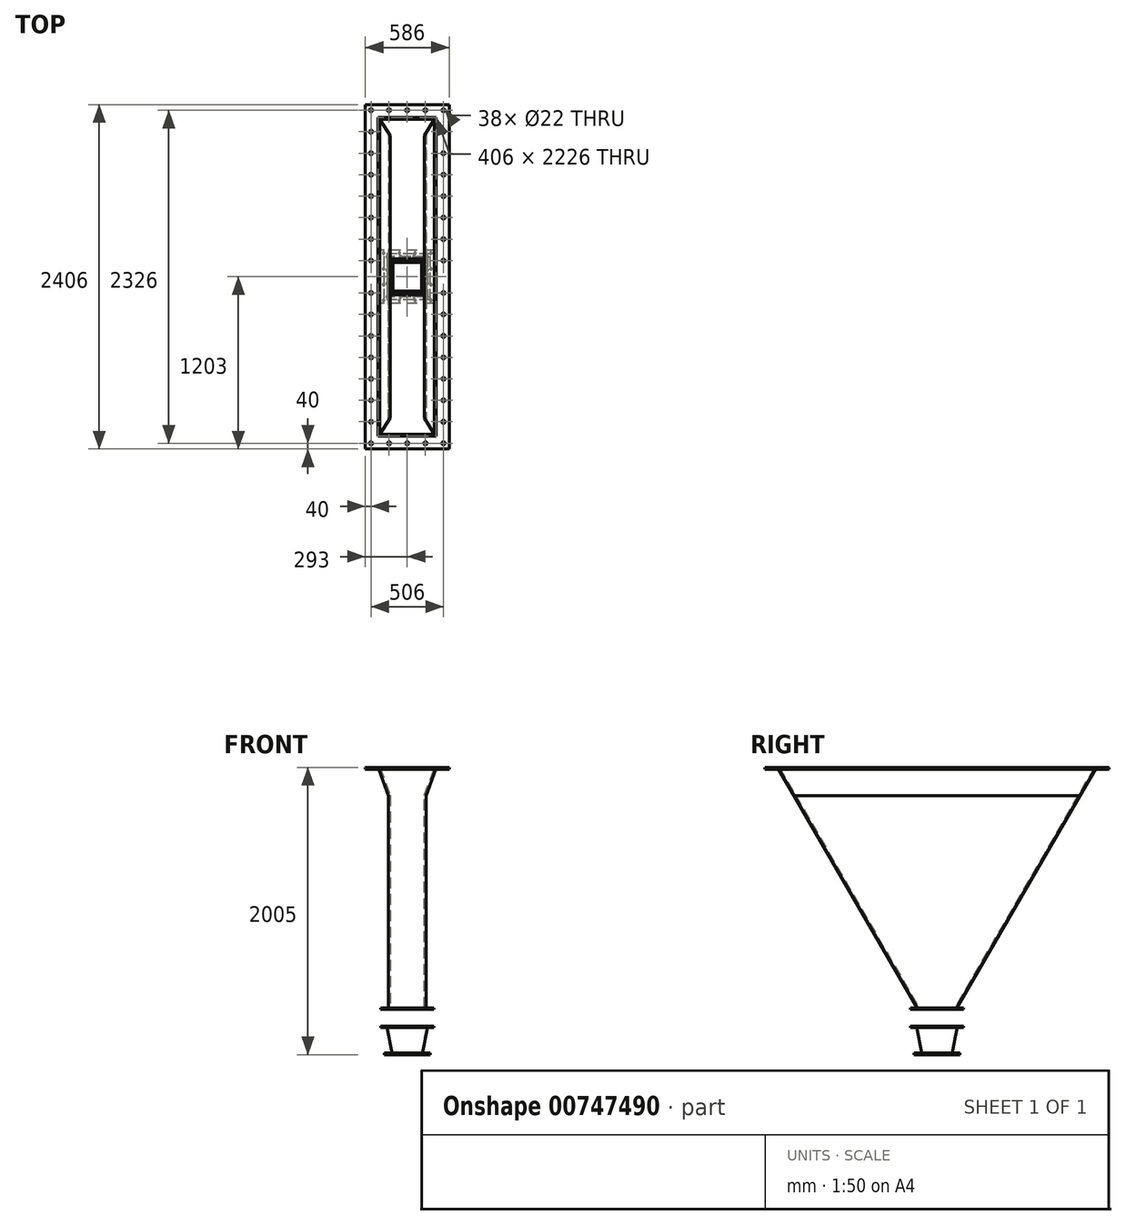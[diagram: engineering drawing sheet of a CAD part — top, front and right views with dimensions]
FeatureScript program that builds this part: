
annotation { "Feature Type Name" : "Feature", "Feature Type Description" : "" }
export const myFeature = defineFeature(function(context is Context, id is Id, definition is map)
    precondition{}
    {
        {
            var Q0;
            Q0=qCreatedBy(makeId("Front.planeOp"),FACE);
            var sketch = newSketch(context, id + "F0", { "sketchPlane" : qUnion([Q0])});
            skLineSegment(sketch, "E0", {"start": v(-203, 0) * mm, "end": v(203, 0) * mm});
            skLineSegment(sketch, "E1", {"start": v(0, 0) * mm, "end": v(0, -195.07) * mm, "construction": true});
            skLineSegment(sketch, "E2", {"start": v(-132, -195.07) * mm, "end": v(132, -195.07) * mm});
            skLineSegment(sketch, "E3", {"start": v(-203, 0) * mm, "end": v(-132, -195.07) * mm});
            skLineSegment(sketch, "E4", {"start": v(132, -195.07) * mm, "end": v(203, 0) * mm});
            skLineSegment(sketch, "E5", {"start": v(-132, -195.07) * mm, "end": v(-132, -1690) * mm});
            skLineSegment(sketch, "E6", {"start": v(-132, -1690) * mm, "end": v(132, -1690) * mm});
            skLineSegment(sketch, "E7", {"start": v(132, -1690) * mm, "end": v(132, -195.07) * mm});
            skLineSegment(sketch, "E8", {"start": v(-132, -195.07) * mm, "end": v(-132, 0) * mm, "construction": true});
            skLineSegment(sketch, "E9", {"start": v(132, -195.07) * mm, "end": v(132, 0) * mm, "construction": true});
            skSolve(sketch);
        }
        {
            var Q0;
            Q0=makeQuery(id+"F0.imprint","IMPRINT",FACE,{"disambiguationData":[TD([[makeQuery(id+"F0.imprint","IMPRINT",EDGE,{"derivedFrom":sQuery(id+"F0.wireOp",EDGE,"E0")}),-1.0]])]});
            var Q1;
            Q1=makeQuery(id+"F0.imprint","IMPRINT",FACE,{"disambiguationData":[TD([[makeQuery(id+"F0.imprint","IMPRINT",EDGE,{"derivedFrom":sQuery(id+"F0.wireOp",EDGE,"E2")}),-1.0]])]});
            extrude(context, id + "F1", {"entities" : qUnion([Q0, Q1]), "endBound" : BoundingType.SYMMETRIC, "oppositeDirection" : true, "depth" : 2226 * mm, "offsetDistance" : 25 * mm});
        }
        {
            var Q0;
            Q0=makeQuery(id+"F1.opExtrude","SWEPT_FACE",FACE,{"disambiguationData":[OSD([sQuery(id+"F0.wireOp",EDGE,"E7")])]});
            var sketch = newSketch(context, id + "F2", { "sketchPlane" : qUnion([Q0])});
            skLineSegment(sketch, "E10", {"start": v(0, -1690) * mm, "end": v(0, -1167.4) * mm, "construction": true});
            skLineSegment(sketch, "E11", {"start": v(0, -1690) * mm, "end": v(132, -1690) * mm});
            skLineSegment(sketch, "E12", {"start": v(132, -1690) * mm, "end": v(1113, 0) * mm});
            skLineSegment(sketch, "E13", {"start": v(1113, 0) * mm, "end": v(1113, -1690) * mm});
            skLineSegment(sketch, "E14", {"start": v(1113, -1690) * mm, "end": v(132, -1690) * mm});
            skLineSegment(sketch, "E15.MirrorCS", {"start": v(-132, -1690) * mm, "end": v(-1113, 0) * mm});
            skLineSegment(sketch, "E16.MirrorCS", {"start": v(-1113, -1690) * mm, "end": v(-132, -1690) * mm});
            skLineSegment(sketch, "E17.MirrorCS", {"start": v(-1113, 0) * mm, "end": v(-1113, -1690) * mm});
            skSolve(sketch);
        }
        {
            var Q0;
            Q0=qSketchRegion(id+"F2",true);
            extrude(context, id + "F3", {"entities" : qUnion([Q0]), "operationType" : NewBodyOperationType.REMOVE, "oppositeDirection" : true, "depth" : 400 * mm, "offsetDistance" : 25 * mm, "hasSecondDirection" : true, "secondDirectionOppositeDirection" : false, "secondDirectionDepth" : 400 * mm});
        }
        {
            var Q0;
            Q0=makeQuery(id+"F1.opExtrude","SWEPT_FACE",FACE,{"disambiguationData":[OSD([sQuery(id+"F0.wireOp",EDGE,"E0")])]});
            shell(context, id + "F4", {"entities" : qUnion([Q0]), "thickness" : 12 * mm});
        }
        {
            var Q0;
            Q0=makeQuery(id+"F1.opExtrude","SWEPT_FACE",FACE,{"disambiguationData":[OSD([sQuery(id+"F0.wireOp",EDGE,"E6")])]});
            var sketch = newSketch(context, id + "F5", { "sketchPlane" : qUnion([Q0])});
            skLineSegment(sketch, "E18.bottom", {"start": v(-120, 120) * mm, "end": v(120, 120) * mm});
            skLineSegment(sketch, "E18.top", {"start": v(-120, -120) * mm, "end": v(120, -120) * mm});
            skLineSegment(sketch, "E18.left", {"start": v(-120, 120) * mm, "end": v(-120, -120) * mm});
            skLineSegment(sketch, "E18.right", {"start": v(120, 120) * mm, "end": v(120, -120) * mm});
            skPoint(sketch, "E18.middle", {"position": v(0, 0) * mm});
            skPoint(sketch, "E18.middle.positionSnap0", {"position": v(132, 0) * mm});
            skPoint(sketch, "E18.middle.positionSnap1", {"position": v(0, -132) * mm});
            skPoint(sketch, "E18.centerSnap0", {"position": v(132, 0) * mm});
            skPoint(sketch, "E18.centerSnap1", {"position": v(0, -132) * mm});
            skSolve(sketch);
        }
        {
            var Q0;
            Q0=qSketchRegion(id+"F5",true);
            extrude(context, id + "F6", {"entities" : qUnion([Q0]), "operationType" : NewBodyOperationType.REMOVE, "endBound" : BoundingType.THROUGH_ALL, "oppositeDirection" : true, "depth" : 25 * mm, "offsetDistance" : 25 * mm});
        }
        {
            var Q0;
            Q0=makeQuery(id+"F1.opExtrude","SWEPT_FACE",FACE,{"disambiguationData":[OSD([sQuery(id+"F0.wireOp",EDGE,"E0")])]});
            var sketch = newSketch(context, id + "F7", { "sketchPlane" : qUnion([Q0])});
            skLineSegment(sketch, "E19.bottom", {"start": v(-203, -1113) * mm, "end": v(203, -1113) * mm});
            skLineSegment(sketch, "E19.top", {"start": v(-203, 1113) * mm, "end": v(203, 1113) * mm});
            skLineSegment(sketch, "E19.left", {"start": v(-203, -1113) * mm, "end": v(-203, 1113) * mm});
            skLineSegment(sketch, "E19.right", {"start": v(203, -1113) * mm, "end": v(203, 1113) * mm});
            skLineSegment(sketch, "E20.bottom", {"start": v(-293, 1203) * mm, "end": v(293, 1203) * mm});
            skLineSegment(sketch, "E20.top", {"start": v(-293, -1203) * mm, "end": v(293, -1203) * mm});
            skLineSegment(sketch, "E20.left", {"start": v(-293, 1203) * mm, "end": v(-293, -1203) * mm});
            skLineSegment(sketch, "E20.right", {"start": v(293, 1203) * mm, "end": v(293, -1203) * mm});
            skPoint(sketch, "E20.middle", {"position": v(0, 0) * mm});
            skPoint(sketch, "E20.middle.positionSnap0", {"position": v(-203, 0) * mm});
            skPoint(sketch, "E20.middle.positionSnap1", {"position": v(0, -1099.12) * mm});
            skPoint(sketch, "E20.centerSnap0", {"position": v(-203, 0) * mm});
            skPoint(sketch, "E20.centerSnap1", {"position": v(0, -1099.12) * mm});
            skCircle(sketch, "E21", {"center": v(0, -1163) * mm, "radius": 11 * mm});
            skCircle(sketch, "E22", {"center": v(127, -1163) * mm, "radius": 11 * mm});
            skCircle(sketch, "E23", {"center": v(253, -1163) * mm, "radius": 11 * mm});
            skCircle(sketch, "E24", {"center": v(253, -1013) * mm, "radius": 11 * mm});
            skCircle(sketch, "E25", {"center": v(253, -113) * mm, "radius": 11 * mm});
            skCircle(sketch, "E26", {"center": v(253, -263) * mm, "radius": 11 * mm});
            skCircle(sketch, "E27", {"center": v(253, -413) * mm, "radius": 11 * mm});
            skCircle(sketch, "E28", {"center": v(253, -563) * mm, "radius": 11 * mm});
            skCircle(sketch, "E29", {"center": v(253, -713) * mm, "radius": 11 * mm});
            skCircle(sketch, "E30", {"center": v(253, -863) * mm, "radius": 11 * mm});
            skLineSegment(sketch, "E31", {"start": v(0, 0) * mm, "end": v(-353.58, 0) * mm, "construction": true});
            skCircle(sketch, "E32.MirrorC", {"center": v(253, 113) * mm, "radius": 11 * mm});
            skCircle(sketch, "E33.MirrorC", {"center": v(253, 263) * mm, "radius": 11 * mm});
            skCircle(sketch, "E34.MirrorC", {"center": v(253, 413) * mm, "radius": 11 * mm});
            skCircle(sketch, "E35.MirrorC", {"center": v(253, 563) * mm, "radius": 11 * mm});
            skCircle(sketch, "E36.MirrorC", {"center": v(253, 713) * mm, "radius": 11 * mm});
            skCircle(sketch, "E37.MirrorC", {"center": v(253, 863) * mm, "radius": 11 * mm});
            skCircle(sketch, "E38.MirrorC", {"center": v(253, 1013) * mm, "radius": 11 * mm});
            skCircle(sketch, "E39.MirrorC", {"center": v(253, 1163) * mm, "radius": 11 * mm});
            skCircle(sketch, "E40.MirrorC", {"center": v(127, 1163) * mm, "radius": 11 * mm});
            skCircle(sketch, "E41.MirrorC", {"center": v(0, 1163) * mm, "radius": 11 * mm});
            skLineSegment(sketch, "E42", {"start": v(0, 1028.55) * mm, "end": v(0, 1182.62) * mm, "construction": true});
            skCircle(sketch, "E43.MirrorC", {"center": v(-127, 1163) * mm, "radius": 11 * mm});
            skCircle(sketch, "E44.MirrorC", {"center": v(-253, 1163) * mm, "radius": 11 * mm});
            skCircle(sketch, "E45.MirrorC", {"center": v(-253, 1013) * mm, "radius": 11 * mm});
            skCircle(sketch, "E46.MirrorC", {"center": v(-253, 863) * mm, "radius": 11 * mm});
            skCircle(sketch, "E47.MirrorC", {"center": v(-253, 713) * mm, "radius": 11 * mm});
            skCircle(sketch, "E48.MirrorC", {"center": v(-253, 563) * mm, "radius": 11 * mm});
            skCircle(sketch, "E49.MirrorC", {"center": v(-253, 413) * mm, "radius": 11 * mm});
            skCircle(sketch, "E50.MirrorC", {"center": v(-253, 263) * mm, "radius": 11 * mm});
            skCircle(sketch, "E51.MirrorC", {"center": v(-253, 113) * mm, "radius": 11 * mm});
            skCircle(sketch, "E52.MirrorC", {"center": v(-253, -113) * mm, "radius": 11 * mm});
            skCircle(sketch, "E53.MirrorC", {"center": v(-253, -263) * mm, "radius": 11 * mm});
            skCircle(sketch, "E54.MirrorC", {"center": v(-253, -413) * mm, "radius": 11 * mm});
            skCircle(sketch, "E55.MirrorC", {"center": v(-253, -563) * mm, "radius": 11 * mm});
            skCircle(sketch, "E56.MirrorC", {"center": v(-253, -713) * mm, "radius": 11 * mm});
            skCircle(sketch, "E57.MirrorC", {"center": v(-253, -863) * mm, "radius": 11 * mm});
            skCircle(sketch, "E58.MirrorC", {"center": v(-253, -1013) * mm, "radius": 11 * mm});
            skCircle(sketch, "E59.MirrorC", {"center": v(-253, -1163) * mm, "radius": 11 * mm});
            skCircle(sketch, "E60.MirrorC", {"center": v(-127, -1163) * mm, "radius": 11 * mm});
            skSolve(sketch);
        }
        {
            var Q0;
            Q0=qSketchRegion(id+"F7",true);
            extrude(context, id + "F8", {"entities" : qUnion([Q0]), "operationType" : NewBodyOperationType.ADD, "oppositeDirection" : true, "depth" : 12 * mm, "offsetDistance" : 25 * mm});
        }
        {
            var Q0;
            Q0=makeQuery(id+"F1.opExtrude","SWEPT_FACE",FACE,{"disambiguationData":[OSD([sQuery(id+"F0.wireOp",EDGE,"E6")])]});
            var sketch = newSketch(context, id + "F9", { "sketchPlane" : qUnion([Q0])});
            skLineSegment(sketch, "E61", {"start": v(0, -943.32) * mm, "end": v(0, -1281.15) * mm, "construction": true});
            skPoint(sketch, "E61.startSnap0", {"position": v(0, 132) * mm});
            skPoint(sketch, "E61.endSnap0", {"position": v(0, -132) * mm});
            skLineSegment(sketch, "E62", {"start": v(143.58, 0) * mm, "end": v(-139.48, 0) * mm, "construction": true});
            skPoint(sketch, "E62.startSnap0", {"position": v(132, 0) * mm});
            skLineSegment(sketch, "E63.bottom", {"start": v(185, -185) * mm, "end": v(-185, -185) * mm});
            skLineSegment(sketch, "E63.top", {"start": v(185, 185) * mm, "end": v(-185, 185) * mm});
            skLineSegment(sketch, "E63.left", {"start": v(185, -185) * mm, "end": v(185, 185) * mm});
            skLineSegment(sketch, "E63.right", {"start": v(-185, -185) * mm, "end": v(-185, 185) * mm});
            skPoint(sketch, "E63.middle", {"position": v(0, 0) * mm});
            skLineSegment(sketch, "E64.bottom", {"start": v(132, -132) * mm, "end": v(-132, -132) * mm});
            skLineSegment(sketch, "E64.top", {"start": v(132, 132) * mm, "end": v(-132, 132) * mm});
            skLineSegment(sketch, "E64.left", {"start": v(132, -132) * mm, "end": v(132, 132) * mm});
            skLineSegment(sketch, "E64.right", {"start": v(-132, -132) * mm, "end": v(-132, 132) * mm});
            skCircle(sketch, "E65", {"center": v(-165, 165) * mm, "radius": 7.5 * mm});
            skCircle(sketch, "E66", {"center": v(-55, 165) * mm, "radius": 7.5 * mm});
            skCircle(sketch, "E67", {"center": v(-165, 55) * mm, "radius": 7.5 * mm});
            skCircle(sketch, "E68.MirrorC", {"center": v(55, 165) * mm, "radius": 7.5 * mm});
            skCircle(sketch, "E69.MirrorC", {"center": v(165, 165) * mm, "radius": 7.5 * mm});
            skCircle(sketch, "E70.MirrorC", {"center": v(165, 55) * mm, "radius": 7.5 * mm});
            skCircle(sketch, "E71.MirrorC", {"center": v(-165, -55) * mm, "radius": 7.5 * mm});
            skCircle(sketch, "E72.MirrorC", {"center": v(-165, -165) * mm, "radius": 7.5 * mm});
            skCircle(sketch, "E73.MirrorC", {"center": v(-55, -165) * mm, "radius": 7.5 * mm});
            skCircle(sketch, "E74.MirrorC", {"center": v(55, -165) * mm, "radius": 7.5 * mm});
            skCircle(sketch, "E75.MirrorC", {"center": v(165, -165) * mm, "radius": 7.5 * mm});
            skCircle(sketch, "E76.MirrorC", {"center": v(165, -55) * mm, "radius": 7.5 * mm});
            skSolve(sketch);
        }
        {
            var Q0;
            Q0=qSketchRegion(id+"F9",true);
            extrude(context, id + "F10", {"entities" : qUnion([Q0]), "operationType" : NewBodyOperationType.ADD, "oppositeDirection" : true, "depth" : 12 * mm, "offsetDistance" : 25 * mm});
        }
        {
            var Q0;
            Q0=makeQuery(id+"F10.boolean.opBoolean","MERGE",FACE,{"derivedFrom":[makeQuery(id+"F1.opExtrude","SWEPT_FACE",FACE,{"disambiguationData":[OSD([sQuery(id+"F0.wireOp",EDGE,"E6")])]}),makeQuery(id+"F10.opExtrude","CAP_FACE",FACE,{"disambiguationData":[OSD([sQuery(id+"F9.wireOp",EDGE,"E63.bottom"),sQuery(id+"F9.wireOp",EDGE,"E63.top"),sQuery(id+"F9.wireOp",EDGE,"E63.left"),sQuery(id+"F9.wireOp",EDGE,"E63.right"),sQuery(id+"F9.wireOp",EDGE,"E64.bottom"),sQuery(id+"F9.wireOp",EDGE,"E64.top"),sQuery(id+"F9.wireOp",EDGE,"E64.left"),sQuery(id+"F9.wireOp",EDGE,"E64.right"),sQuery(id+"F9.wireOp",EDGE,"E65"),sQuery(id+"F9.wireOp",EDGE,"E66"),sQuery(id+"F9.wireOp",EDGE,"E67"),sQuery(id+"F9.wireOp",EDGE,"E68.MirrorC"),sQuery(id+"F9.wireOp",EDGE,"E69.MirrorC"),sQuery(id+"F9.wireOp",EDGE,"E70.MirrorC"),sQuery(id+"F9.wireOp",EDGE,"E71.MirrorC"),sQuery(id+"F9.wireOp",EDGE,"E72.MirrorC"),sQuery(id+"F9.wireOp",EDGE,"E73.MirrorC"),sQuery(id+"F9.wireOp",EDGE,"E74.MirrorC"),sQuery(id+"F9.wireOp",EDGE,"E75.MirrorC"),sQuery(id+"F9.wireOp",EDGE,"E76.MirrorC")])],"isStart":true})]});
            cPlane(context, id + "F11", {"entities" : qUnion([Q0]), "cplaneType" : CPlaneType.OFFSET, "offset" : 115 * mm, "width" : 150 * mm, "height" : 150 * mm});
        }
        {
            var Q0;
            Q0=qCreatedBy(id+"F11.planeOp",FACE);
            var sketch = newSketch(context, id + "F12", { "sketchPlane" : qUnion([Q0])});
            skLineSegment(sketch, "E77.bottom", {"start": v(185, 185) * mm, "end": v(-185, 185) * mm});
            skLineSegment(sketch, "E77.top", {"start": v(185, -185) * mm, "end": v(-185, -185) * mm});
            skLineSegment(sketch, "E77.left", {"start": v(185, 185) * mm, "end": v(185, -185) * mm});
            skLineSegment(sketch, "E77.right", {"start": v(-185, 185) * mm, "end": v(-185, -185) * mm});
            skPoint(sketch, "E77.middle", {"position": v(0, 0) * mm});
            skLineSegment(sketch, "E78.bottom", {"start": v(137.5, 137.5) * mm, "end": v(-137.5, 137.5) * mm});
            skLineSegment(sketch, "E78.top", {"start": v(137.5, -137.5) * mm, "end": v(-137.5, -137.5) * mm});
            skLineSegment(sketch, "E78.left", {"start": v(137.5, 137.5) * mm, "end": v(137.5, -137.5) * mm});
            skLineSegment(sketch, "E78.right", {"start": v(-137.5, 137.5) * mm, "end": v(-137.5, -137.5) * mm});
            skCircle(sketch, "E79", {"center": v(-165, 165) * mm, "radius": 7.5 * mm});
            skCircle(sketch, "E80", {"center": v(-55, 164.99) * mm, "radius": 7.5 * mm});
            skCircle(sketch, "E81", {"center": v(-165, 55) * mm, "radius": 7.5 * mm});
            skCircle(sketch, "E82.MirrorC", {"center": v(55, 164.99) * mm, "radius": 7.5 * mm});
            skCircle(sketch, "E83.MirrorC", {"center": v(165, 165) * mm, "radius": 7.5 * mm});
            skCircle(sketch, "E84.MirrorC", {"center": v(165, 55) * mm, "radius": 7.5 * mm});
            skCircle(sketch, "E85.MirrorC", {"center": v(-165, -55) * mm, "radius": 7.5 * mm});
            skCircle(sketch, "E86.MirrorC", {"center": v(165, -55) * mm, "radius": 7.5 * mm});
            skCircle(sketch, "E87.MirrorC", {"center": v(165, -165) * mm, "radius": 7.5 * mm});
            skCircle(sketch, "E88.MirrorC", {"center": v(55, -164.99) * mm, "radius": 7.5 * mm});
            skCircle(sketch, "E89.MirrorC", {"center": v(-55, -164.99) * mm, "radius": 7.5 * mm});
            skCircle(sketch, "E90.MirrorC", {"center": v(-165, -165) * mm, "radius": 7.5 * mm});
            skLineSegment(sketch, "E91", {"start": v(0, 278.52) * mm, "end": v(0, -477.62) * mm, "construction": true});
            skSolve(sketch);
        }
        {
            var Q0;
            Q0 = qSketchRegion(id + "F12", true);
            extrude(context, id + "F13", {"entities" : qUnion([Q0]), "depth" : 12 * mm, "offsetDistance" : 25 * mm});
        }
        {
            var Q0;
            Q0=qCreatedBy(id+"F11.planeOp",FACE);
            var Q1;
            Q1=sQuery(id+"F12.wireOp",EDGE,"E91");
            cPlane(context, id + "F14", {"entities" : qUnion([Q0, Q1]), "cplaneType" : CPlaneType.LINE_ANGLE, "offset" : 25 * mm, "angle" : 90 * degree, "width" : 150 * mm, "height" : 150 * mm});
        }
        {
            var Q0;
            Q0=qCreatedBy(id+"F14.planeOp",FACE);
            var sketch = newSketch(context, id + "F15", { "sketchPlane" : qUnion([Q0])});
            skLineSegment(sketch, "E92", {"start": v(0, -1693.72) * mm, "end": v(0, -1817) * mm, "construction": true});
            skLineSegment(sketch, "E93", {"start": v(0, -1817) * mm, "end": v(-142.5, -1817) * mm, "construction": true});
            skLineSegment(sketch, "E94", {"start": v(-142.5, -1817) * mm, "end": v(142.5, -1817) * mm, "construction": true});
            skLineSegment(sketch, "E95", {"start": v(142.5, -1817) * mm, "end": v(-142.5, -1817) * mm});
            skLineSegment(sketch, "E96", {"start": v(142.5, -1817) * mm, "end": v(105, -2005) * mm});
            skLineSegment(sketch, "E97", {"start": v(105, -2005) * mm, "end": v(-105, -2005) * mm});
            skLineSegment(sketch, "E98", {"start": v(-105, -2005) * mm, "end": v(-142.5, -1817) * mm});
            skSolve(sketch);
        }
        {
            var Q0;
            Q0 = qSketchRegion(id + "F15", true);
            extrude(context, id + "F16", {"entities" : qUnion([Q0]), "endBound" : BoundingType.SYMMETRIC, "depth" : 285 * mm, "offsetDistance" : 25 * mm});
        }
        {
            var Q0;
            Q0=qCreatedBy(id+"F14.planeOp",FACE);
            var Q1;
            Q1=sQuery(id+"F15.wireOp",EDGE,"E92");
            cPlane(context, id + "F17", {"entities" : qUnion([Q0, Q1]), "cplaneType" : CPlaneType.LINE_ANGLE, "offset" : 25 * mm, "angle" : 90 * degree, "width" : 150 * mm, "height" : 150 * mm});
        }
        {
            var Q0;
            Q0=qCreatedBy(id+"F17.planeOp",FACE);
            var sketch = newSketch(context, id + "F18", { "sketchPlane" : qUnion([Q0])});
            skLineSegment(sketch, "E99", {"start": v(142.5, -1817) * mm, "end": v(142.5, -2005) * mm});
            skLineSegment(sketch, "E100.MirrorCS", {"start": v(-142.5, -1817) * mm, "end": v(-142.5, -2005) * mm});
            skLineSegment(sketch, "E101", {"start": v(142.5, -1817) * mm, "end": v(105, -2005) * mm});
            skLineSegment(sketch, "E102", {"start": v(-105, -2005) * mm, "end": v(-142.5, -1817) * mm});
            skLineSegment(sketch, "E103", {"start": v(142.5, -2005) * mm, "end": v(105, -2005) * mm});
            skLineSegment(sketch, "E104", {"start": v(-105, -2005) * mm, "end": v(-142.5, -2005) * mm});
            skSolve(sketch);
        }
        {
            var Q0;
            Q0 = qSketchRegion(id + "F18", true);
            extrude(context, id + "F19", {"entities" : qUnion([Q0]), "operationType" : NewBodyOperationType.REMOVE, "endBound" : BoundingType.SYMMETRIC, "oppositeDirection" : true, "depth" : 285 * mm, "offsetDistance" : 25 * mm});
        }
        {
            var Q0;
            Q0=makeQuery(id+"F16.opExtrude","SWEPT_FACE",FACE,{"disambiguationData":[OSD([sQuery(id+"F15.wireOp",EDGE,"E95")])]});
            shell(context, id + "F20", {"entities" : qUnion([Q0]), "thickness" : 5 * mm});
        }
        {
            var Q0;
            Q0=makeQuery(id+"F16.opExtrude","SWEPT_FACE",FACE,{"disambiguationData":[OSD([sQuery(id+"F15.wireOp",EDGE,"E97")])]});
            var sketch = newSketch(context, id + "F21", { "sketchPlane" : qUnion([Q0])});
            skLineSegment(sketch, "E105.bottom", {"start": v(100, 100) * mm, "end": v(-100, 100) * mm});
            skLineSegment(sketch, "E105.top", {"start": v(100, -100) * mm, "end": v(-100, -100) * mm});
            skLineSegment(sketch, "E105.left", {"start": v(100, 100) * mm, "end": v(100, -100) * mm});
            skLineSegment(sketch, "E105.right", {"start": v(-100, 100) * mm, "end": v(-100, -100) * mm});
            skPoint(sketch, "E105.middle", {"position": v(0, 0) * mm});
            skSolve(sketch);
        }
        {
            var Q0;
            Q0 = qSketchRegion(id + "F21", true);
            extrude(context, id + "F22", {"entities" : qUnion([Q0]), "operationType" : NewBodyOperationType.REMOVE, "oppositeDirection" : true, "depth" : 10 * mm, "offsetDistance" : 25 * mm});
        }
        {
            var Q0;
            Q0=makeQuery(id+"F16.opExtrude","SWEPT_FACE",FACE,{"disambiguationData":[OSD([sQuery(id+"F15.wireOp",EDGE,"E97")])]});
            var sketch = newSketch(context, id + "F23", { "sketchPlane" : qUnion([Q0])});
            skLineSegment(sketch, "E106.bottom", {"start": v(160, 160) * mm, "end": v(-160, 160) * mm});
            skLineSegment(sketch, "E106.top", {"start": v(160, -160) * mm, "end": v(-160, -160) * mm});
            skLineSegment(sketch, "E106.left", {"start": v(160, 160) * mm, "end": v(160, -160) * mm});
            skLineSegment(sketch, "E106.right", {"start": v(-160, 160) * mm, "end": v(-160, -160) * mm});
            skPoint(sketch, "E106.middle", {"position": v(0, 0) * mm});
            skLineSegment(sketch, "E107.bottom", {"start": v(105, 105) * mm, "end": v(-105, 105) * mm});
            skLineSegment(sketch, "E107.top", {"start": v(105, -105) * mm, "end": v(-105, -105) * mm});
            skLineSegment(sketch, "E107.left", {"start": v(105, 105) * mm, "end": v(105, -105) * mm});
            skLineSegment(sketch, "E107.right", {"start": v(-105, 105) * mm, "end": v(-105, -105) * mm});
            skCircle(sketch, "E108", {"center": v(-140, -140) * mm, "radius": 7.5 * mm});
            skCircle(sketch, "E109", {"center": v(-46.7, -140) * mm, "radius": 7.5 * mm});
            skCircle(sketch, "E110", {"center": v(-140, -46.7) * mm, "radius": 7.5 * mm});
            skCircle(sketch, "E111.MirrorC", {"center": v(46.7, -140) * mm, "radius": 7.5 * mm});
            skCircle(sketch, "E112.MirrorC", {"center": v(140, -140) * mm, "radius": 7.5 * mm});
            skCircle(sketch, "E113.MirrorC", {"center": v(-140, 46.7) * mm, "radius": 7.5 * mm});
            skCircle(sketch, "E114.MirrorC", {"center": v(-46.7, 140) * mm, "radius": 7.5 * mm});
            skCircle(sketch, "E115.MirrorC", {"center": v(-140, 140) * mm, "radius": 7.5 * mm});
            skCircle(sketch, "E116.MirrorC", {"center": v(46.7, 140) * mm, "radius": 7.5 * mm});
            skCircle(sketch, "E117.MirrorC", {"center": v(140, 140) * mm, "radius": 7.5 * mm});
            skCircle(sketch, "E118.MirrorC", {"center": v(140, 46.7) * mm, "radius": 7.5 * mm});
            skCircle(sketch, "E119.MirrorC", {"center": v(140, -46.7) * mm, "radius": 7.5 * mm});
            skSolve(sketch);
        }
        {
            var Q0;
            Q0 = qSketchRegion(id + "F23", true);
            extrude(context, id + "F24", {"entities" : qUnion([Q0]), "operationType" : NewBodyOperationType.ADD, "oppositeDirection" : true, "depth" : 12 * mm, "offsetDistance" : 25 * mm});
        }
    });
